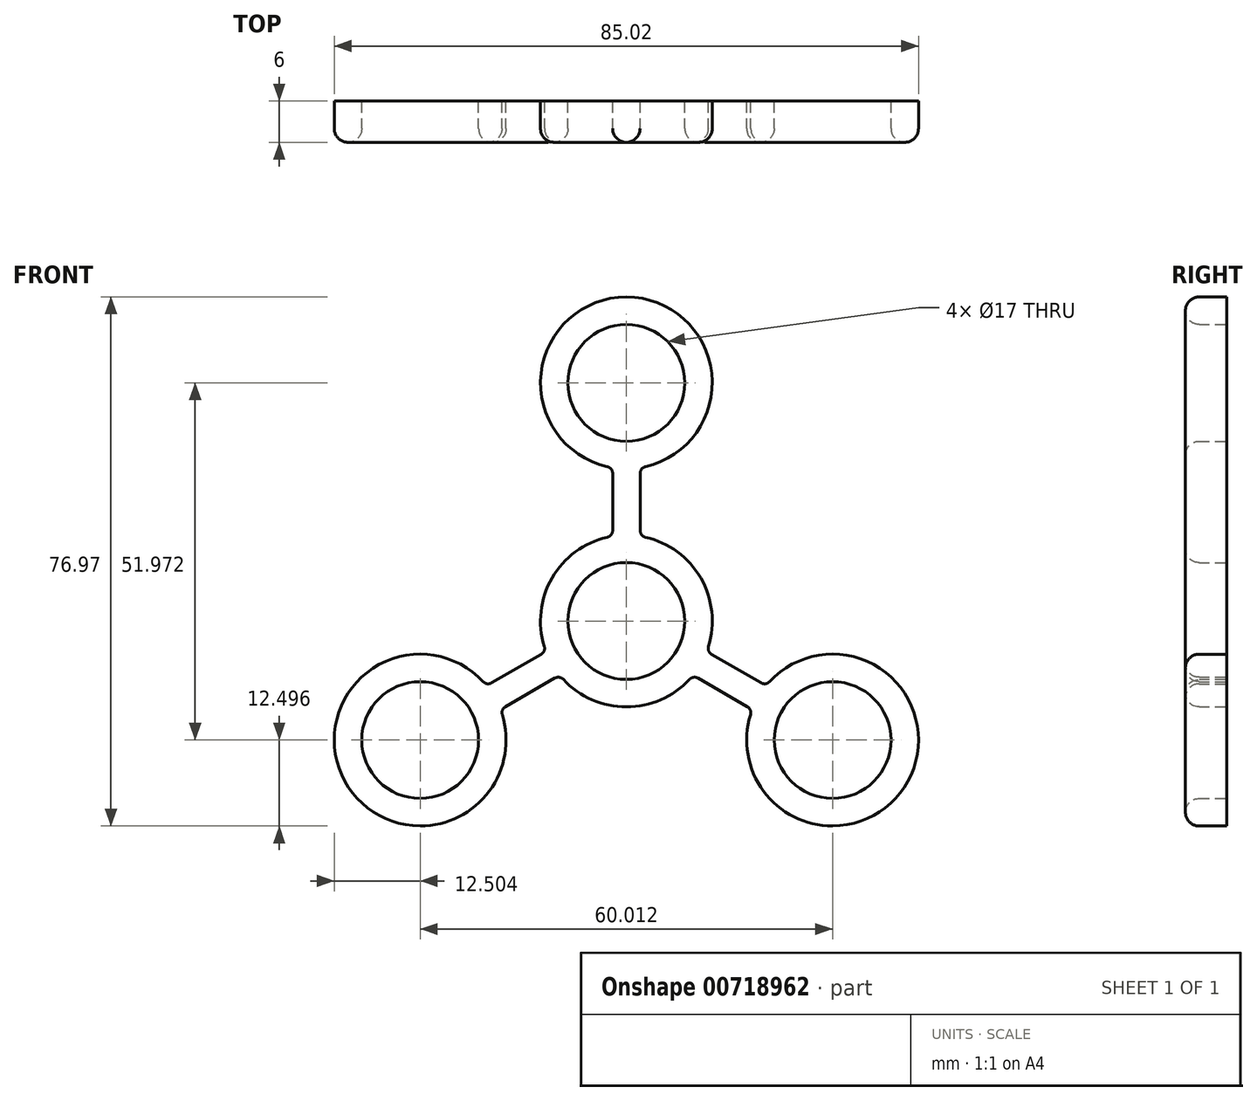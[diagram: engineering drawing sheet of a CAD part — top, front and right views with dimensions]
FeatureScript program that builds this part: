
annotation { "Feature Type Name" : "Feature", "Feature Type Description" : "" }
export const myFeature = defineFeature(function(context is Context, id is Id, definition is map)
    precondition{}
    {
        {
            var Q0;
            Q0=qCreatedBy(makeId("Front.planeOp"),FACE);
            var sketch = newSketch(context, id + "F0", { "sketchPlane" : qUnion([Q0])});
            skCircle(sketch, "E0", {"center": v(0, 0) * mm, "radius": 8.5 * mm});
            skArc(sketch, "E1.0", {"start": v(11.94, -3.69) * mm, "mid": v(10.83, 6.25) * mm, "end": v(2.78, 12.19) * mm});
            skCircle(sketch, "E2", {"center": v(0, 34.65) * mm, "radius": 8.5 * mm});
            skArc(sketch, "E3.0", {"start": v(2.78, 22.46) * mm, "mid": v(0, 47.15) * mm, "end": v(-2.78, 22.46) * mm});
            skArc(sketch, "E4.1.0", {"start": v(-20.84, -8.82) * mm, "mid": v(-40.83, -23.57) * mm, "end": v(-18.06, -13.64) * mm});
            skArc(sketch, "E4.2.0", {"start": v(18.06, -13.64) * mm, "mid": v(40.83, -23.57) * mm, "end": v(20.84, -8.82) * mm});
            skLineSegment(sketch, "E5", {"start": v(-2, 21.49) * mm, "end": v(-2, 13.16) * mm});
            skLineSegment(sketch, "E6", {"start": v(0, 22.15) * mm, "end": v(0, 12.5) * mm, "construction": true});
            skLineSegment(sketch, "E7.MirrorCS", {"start": v(2, 21.49) * mm, "end": v(2, 13.16) * mm});
            skLineSegment(sketch, "E8.1.0", {"start": v(-17.6, -12.47) * mm, "end": v(-10.4, -8.31) * mm});
            skLineSegment(sketch, "E8.1.1", {"start": v(-19.6, -9.01) * mm, "end": v(-12.4, -4.85) * mm});
            skLineSegment(sketch, "E8.2.0", {"start": v(19.6, -9.01) * mm, "end": v(12.4, -4.85) * mm});
            skLineSegment(sketch, "E8.2.1", {"start": v(17.6, -12.47) * mm, "end": v(10.4, -8.31) * mm});
            skCircle(sketch, "E9.1.0", {"center": v(-30, -17.32) * mm, "radius": 8.5 * mm});
            skCircle(sketch, "E9.2.0", {"center": v(30, -17.32) * mm, "radius": 8.5 * mm});
            skArc(sketch, "E10.trimOffspring", {"start": v(-9.17, -8.5) * mm, "mid": v(0, -12.5) * mm, "end": v(9.17, -8.5) * mm});
            skArc(sketch, "E11.trimOffspring", {"start": v(-2.78, 12.19) * mm, "mid": v(-10.83, 6.25) * mm, "end": v(-11.94, -3.69) * mm});
            skPoint(sketch, "E12.visualSharp", {"position": v(2, 22.3) * mm});
            skArc(sketch, "E12.filletArc", {"start": v(2.78, 22.46) * mm, "mid": v(2.22, 22.1) * mm, "end": v(2, 21.49) * mm});
            skPoint(sketch, "E13.visualSharp", {"position": v(-2, 22.3) * mm});
            skArc(sketch, "E13.filletArc", {"start": v(-2, 21.49) * mm, "mid": v(-2.22, 22.1) * mm, "end": v(-2.78, 22.46) * mm});
            skPoint(sketch, "E14.visualSharp", {"position": v(-2, 12.34) * mm});
            skArc(sketch, "E14.filletArc", {"start": v(-2.78, 12.19) * mm, "mid": v(-2.22, 12.54) * mm, "end": v(-2, 13.16) * mm});
            skPoint(sketch, "E15.visualSharp", {"position": v(2, 12.34) * mm});
            skArc(sketch, "E15.filletArc", {"start": v(2, 13.16) * mm, "mid": v(2.22, 12.54) * mm, "end": v(2.78, 12.19) * mm});
            skPoint(sketch, "E16.visualSharp", {"position": v(-11.69, -4.44) * mm});
            skArc(sketch, "E16.filletArc", {"start": v(-12.4, -4.85) * mm, "mid": v(-11.97, -4.35) * mm, "end": v(-11.94, -3.69) * mm});
            skPoint(sketch, "E17.visualSharp", {"position": v(-20.32, -9.42) * mm});
            skArc(sketch, "E17.filletArc", {"start": v(-20.84, -8.82) * mm, "mid": v(-20.26, -9.13) * mm, "end": v(-19.6, -9.01) * mm});
            skPoint(sketch, "E18.visualSharp", {"position": v(-18.32, -12.89) * mm});
            skArc(sketch, "E18.filletArc", {"start": v(-17.6, -12.47) * mm, "mid": v(-18.04, -12.98) * mm, "end": v(-18.06, -13.64) * mm});
            skPoint(sketch, "E19.visualSharp", {"position": v(-9.69, -7.9) * mm});
            skArc(sketch, "E19.filletArc", {"start": v(-9.17, -8.5) * mm, "mid": v(-9.75, -8.2) * mm, "end": v(-10.4, -8.31) * mm});
            skPoint(sketch, "E20.visualSharp", {"position": v(9.69, -7.9) * mm});
            skArc(sketch, "E20.filletArc", {"start": v(10.4, -8.31) * mm, "mid": v(9.75, -8.2) * mm, "end": v(9.17, -8.5) * mm});
            skPoint(sketch, "E21.visualSharp", {"position": v(11.69, -4.44) * mm});
            skArc(sketch, "E21.filletArc", {"start": v(11.94, -3.69) * mm, "mid": v(11.97, -4.35) * mm, "end": v(12.4, -4.85) * mm});
            skPoint(sketch, "E22.visualSharp", {"position": v(20.32, -9.42) * mm});
            skArc(sketch, "E22.filletArc", {"start": v(19.6, -9.01) * mm, "mid": v(20.26, -9.13) * mm, "end": v(20.84, -8.82) * mm});
            skPoint(sketch, "E23.visualSharp", {"position": v(18.32, -12.89) * mm});
            skArc(sketch, "E23.filletArc", {"start": v(18.06, -13.64) * mm, "mid": v(18.04, -12.98) * mm, "end": v(17.6, -12.47) * mm});
            skSolve(sketch);
        }
        {
            var Q0;
            Q0=makeQuery(id+"F0.imprint","IMPRINT",FACE,{"disambiguationData":[TD([[makeQuery(id+"F0.imprint","IMPRINT",EDGE,{"derivedFrom":sQuery(id+"F0.wireOp",EDGE,"E0")}),-1.0]])]});
            extrude(context, id + "F1", {"entities" : qUnion([Q0]), "endBound" : BoundingType.SYMMETRIC, "depth" : 6 * mm, "offsetDistance" : 25.4 * mm});
        }
        {
            var Q0;
            Q0=makeQuery(id+"F1.opExtrude","CAP_FACE",FACE,{"disambiguationData":[OSD([sQuery(id+"F0.wireOp",EDGE,"E0"),sQuery(id+"F0.wireOp",EDGE,"E1.0"),sQuery(id+"F0.wireOp",EDGE,"E2"),sQuery(id+"F0.wireOp",EDGE,"E3.0"),sQuery(id+"F0.wireOp",EDGE,"E4.1.0"),sQuery(id+"F0.wireOp",EDGE,"E4.2.0"),sQuery(id+"F0.wireOp",EDGE,"E5"),sQuery(id+"F0.wireOp",EDGE,"E7.MirrorCS"),sQuery(id+"F0.wireOp",EDGE,"E8.1.0"),sQuery(id+"F0.wireOp",EDGE,"E8.1.1"),sQuery(id+"F0.wireOp",EDGE,"E8.2.0"),sQuery(id+"F0.wireOp",EDGE,"E8.2.1"),sQuery(id+"F0.wireOp",EDGE,"E9.1.0"),sQuery(id+"F0.wireOp",EDGE,"E9.2.0"),sQuery(id+"F0.wireOp",EDGE,"E10.trimOffspring"),sQuery(id+"F0.wireOp",EDGE,"E11.trimOffspring"),sQuery(id+"F0.wireOp",EDGE,"E12.filletArc"),sQuery(id+"F0.wireOp",EDGE,"E13.filletArc"),sQuery(id+"F0.wireOp",EDGE,"E14.filletArc"),sQuery(id+"F0.wireOp",EDGE,"E15.filletArc"),sQuery(id+"F0.wireOp",EDGE,"E16.filletArc"),sQuery(id+"F0.wireOp",EDGE,"E17.filletArc"),sQuery(id+"F0.wireOp",EDGE,"E18.filletArc"),sQuery(id+"F0.wireOp",EDGE,"E19.filletArc"),sQuery(id+"F0.wireOp",EDGE,"E20.filletArc"),sQuery(id+"F0.wireOp",EDGE,"E21.filletArc"),sQuery(id+"F0.wireOp",EDGE,"E22.filletArc"),sQuery(id+"F0.wireOp",EDGE,"E23.filletArc")])],"isStart":false});
            var Q1;
            Q1=makeQuery(id+"F1.opExtrude","CAP_EDGE",EDGE,{"disambiguationData":[OSD([sQuery(id+"F0.wireOp",EDGE,"E9.2.0")])],"isStart":false});
            fillet(context, id + "F2", {"entities" : qUnion([Q0, Q1]), "radius" : 2 * mm, "tangentPropagation" : true, "allowEdgeOverflow" : false});
        }
    });
